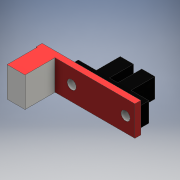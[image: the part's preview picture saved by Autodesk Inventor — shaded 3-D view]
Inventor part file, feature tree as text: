
AUTODESK INVENTOR PART (.ipt)
format: ipt  version: 2016 SP1 (Build 200210100, 210)  size: 161,792 bytes
history: native  units: mm
features: extrude x4, sketch x3
ambient origin geometry x8: Origin, YZ Plane, XZ Plane, XY Plane, X Axis, Y Axis, Z Axis, Center Point
bodies: Solid1 (feature_tree)
feature tree (7):
  extrude  "Extrusion1"  Depth=6.0mm
  extrude  "Extrusion2"  Depth=4.4mm
  extrude  "Extrusion3"  Depth=4.4mm
  extrude  "Extrusion4"  Depth=6.0mm
  sketch  "Sketch1"  dims[d0=3.0mm d1=6.0mm]
  sketch  "Sketch3"  dims[d2=8.0mm d3=4.4mm]
  sketch  "Sketch4"  dims[d4=2.8mm d5=4.4mm d6=6.0mm d7=1.4mm d8=0.0mm d9=6.5mm d10=0.0mm d11=3.0mm d12=3.0mm d13=18.0mm d14=23.6mm d15=2.8mm d16=6.5mm d17=3.25mm d18=3.25mm d19=6.5mm d20=0.0mm d21=10.0mm d22=33.0mm d23=0.3mm d24=6.5mm d25=1.75mm d26=2.0mm d27=0.0mm d28=10.0mm d29=6.0mm d30=0.0mm d31=0.3mm d32=10.0mm d33=0.0mm d34=2.8mm d35=1.4mm]
